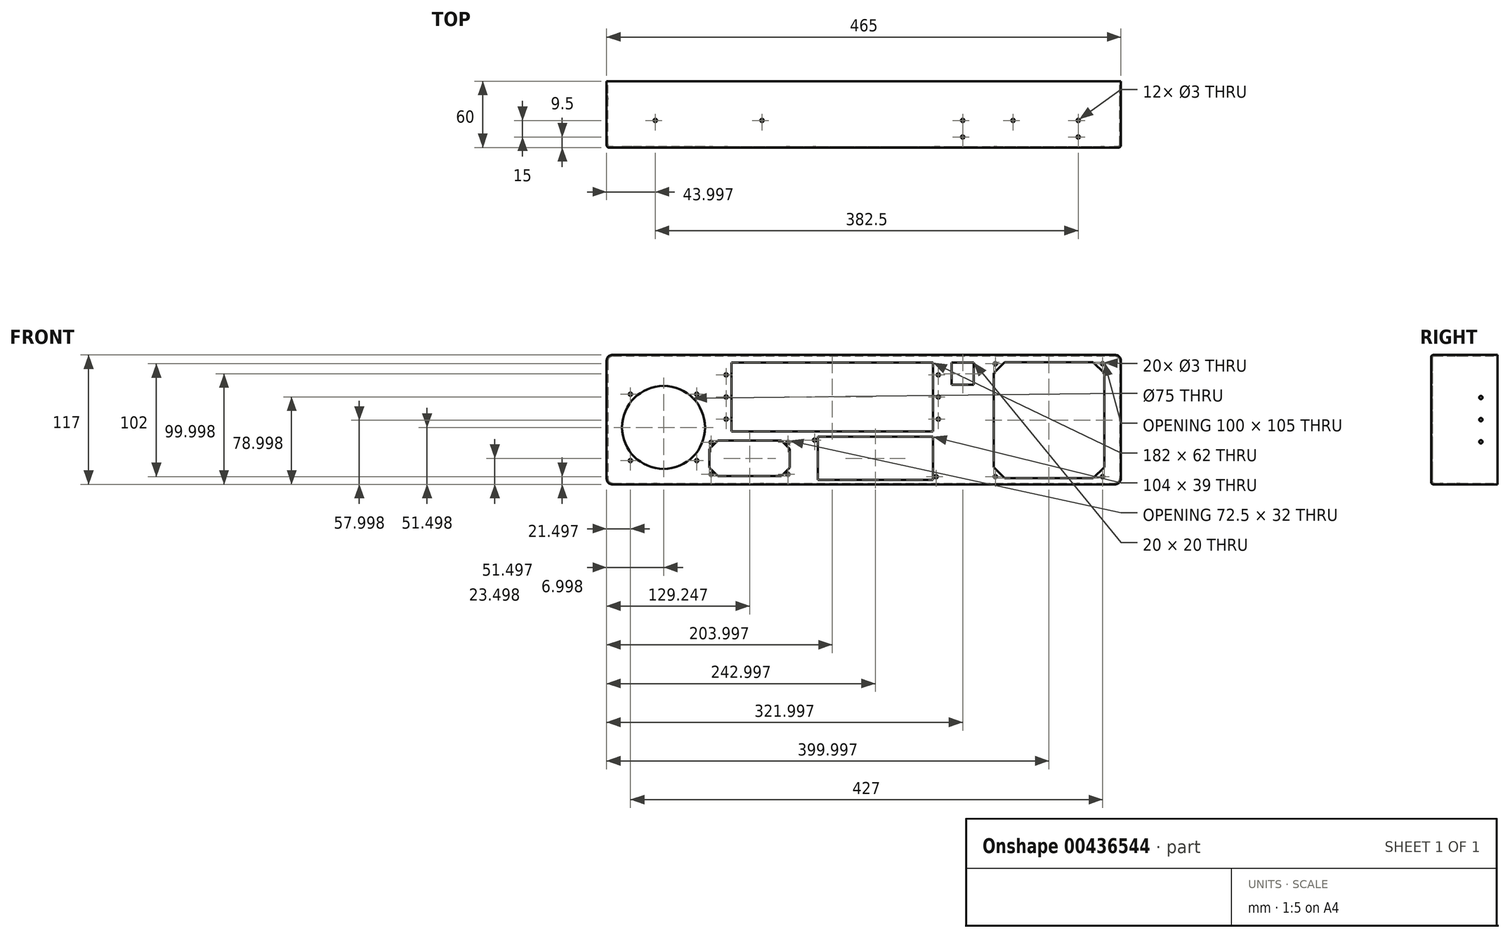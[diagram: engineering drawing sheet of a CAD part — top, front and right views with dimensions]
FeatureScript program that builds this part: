
annotation { "Feature Type Name" : "Feature", "Feature Type Description" : "" }
export const myFeature = defineFeature(function(context is Context, id is Id, definition is map)
    precondition{}
    {
        {
            var Q0;
            Q0=qCreatedBy(makeId("Front.planeOp"),FACE);
            var sketch = newSketch(context, id + "F0", { "sketchPlane" : qUnion([Q0])});
            skLineSegment(sketch, "E0.bottom", {"start": v(-245.15, 85.69) * mm, "end": v(219.85, 85.69) * mm});
            skLineSegment(sketch, "E0.top", {"start": v(-245.15, -31.31) * mm, "end": v(219.85, -31.31) * mm});
            skLineSegment(sketch, "E0.left", {"start": v(-245.15, 85.69) * mm, "end": v(-245.15, -31.31) * mm});
            skLineSegment(sketch, "E0.right", {"start": v(219.85, 85.69) * mm, "end": v(219.85, -31.31) * mm});
            skSolve(sketch);
        }
        {
            var Q0;
            Q0=qSketchRegion(id+"F0",true);
            var Q1;
            Q1=makeQuery(id+"F0.imprint","IMPRINT",FACE,{"disambiguationData":[TD([[makeQuery(id+"F0.imprint","IMPRINT",EDGE,{"derivedFrom":sQuery(id+"F0.wireOp",EDGE,"E0.bottom")}),-1.0]])]});
            extrude(context, id + "F1", {"entities" : qUnion([Q0, Q1]), "depth" : 60 * mm});
        }
        {
            var Q0;
            Q0=makeQuery(id+"F1.opExtrude","CAP_FACE",FACE,{"disambiguationData":[OSD([sQuery(id+"F0.wireOp",EDGE,"E0.bottom"),sQuery(id+"F0.wireOp",EDGE,"E0.top"),sQuery(id+"F0.wireOp",EDGE,"E0.left"),sQuery(id+"F0.wireOp",EDGE,"E0.right")])],"isStart":true});
            shell(context, id + "F2", {"entities" : qUnion([Q0]), "thickness" : 1 * mm});
        }
        {
            var Q0;
            Q0=makeQuery(id+"F1.opExtrude","CAP_FACE",FACE,{"disambiguationData":[OSD([sQuery(id+"F0.wireOp",EDGE,"E0.bottom"),sQuery(id+"F0.wireOp",EDGE,"E0.top"),sQuery(id+"F0.wireOp",EDGE,"E0.left"),sQuery(id+"F0.wireOp",EDGE,"E0.right")])],"isStart":false});
            var sketch = newSketch(context, id + "F3", { "sketchPlane" : qUnion([Q0])});
            skLineSegment(sketch, "E1.bottom", {"start": v(-132.15, 78.69) * mm, "end": v(49.85, 78.69) * mm});
            skLineSegment(sketch, "E1.top", {"start": v(-132.15, 16.69) * mm, "end": v(49.85, 16.69) * mm});
            skLineSegment(sketch, "E1.left", {"start": v(-132.15, 78.69) * mm, "end": v(-132.15, 16.69) * mm});
            skLineSegment(sketch, "E1.right", {"start": v(49.85, 78.69) * mm, "end": v(49.85, 16.69) * mm});
            skLineSegment(sketch, "E2.bottom", {"start": v(66.85, 78.69) * mm, "end": v(86.85, 78.69) * mm});
            skLineSegment(sketch, "E2.top", {"start": v(66.85, 58.69) * mm, "end": v(86.85, 58.69) * mm});
            skLineSegment(sketch, "E2.left", {"start": v(66.85, 78.69) * mm, "end": v(66.85, 58.69) * mm});
            skLineSegment(sketch, "E2.right", {"start": v(86.85, 78.69) * mm, "end": v(86.85, 58.69) * mm});
            skLineSegment(sketch, "E3.bottom", {"start": v(114.85, 79.19) * mm, "end": v(194.85, 79.19) * mm});
            skLineSegment(sketch, "E3.top", {"start": v(114.85, -25.81) * mm, "end": v(194.85, -25.81) * mm});
            skLineSegment(sketch, "E3.left", {"start": v(104.85, 69.19) * mm, "end": v(104.85, -15.81) * mm});
            skLineSegment(sketch, "E3.right", {"start": v(204.85, 69.19) * mm, "end": v(204.85, -15.81) * mm});
            skCircle(sketch, "E4", {"center": v(54.85, 67.69) * mm, "radius": 1.5 * mm});
            skCircle(sketch, "E5", {"center": v(54.85, 47.69) * mm, "radius": 1.5 * mm});
            skCircle(sketch, "E6", {"center": v(54.85, 27.69) * mm, "radius": 1.5 * mm});
            skCircle(sketch, "E7", {"center": v(106.35, 77.69) * mm, "radius": 1.5 * mm});
            skLineSegment(sketch, "E8", {"start": v(104.85, 69.19) * mm, "end": v(114.85, 79.19) * mm});
            skLineSegment(sketch, "E9.bottom", {"start": v(-144.65, 8.19) * mm, "end": v(-87.15, 8.19) * mm});
            skLineSegment(sketch, "E9.top", {"start": v(-144.65, -23.81) * mm, "end": v(-87.15, -23.81) * mm});
            skLineSegment(sketch, "E9.left", {"start": v(-152.15, 0.69) * mm, "end": v(-152.15, -16.31) * mm});
            skLineSegment(sketch, "E9.right", {"start": v(-79.65, 0.69) * mm, "end": v(-79.65, -16.31) * mm});
            skLineSegment(sketch, "E10", {"start": v(104.85, -15.81) * mm, "end": v(114.85, -25.81) * mm});
            skLineSegment(sketch, "E11", {"start": v(194.85, -25.81) * mm, "end": v(204.85, -15.81) * mm});
            skLineSegment(sketch, "E12", {"start": v(194.85, 79.19) * mm, "end": v(204.85, 69.19) * mm});
            skCircle(sketch, "E13", {"center": v(-193.65, 20.19) * mm, "radius": 37.5 * mm});
            skLineSegment(sketch, "E14", {"start": v(-152.15, 0.69) * mm, "end": v(-144.65, 8.19) * mm});
            skLineSegment(sketch, "E15", {"start": v(-87.15, 8.19) * mm, "end": v(-79.65, 0.69) * mm});
            skLineSegment(sketch, "E16", {"start": v(-79.65, -16.31) * mm, "end": v(-87.15, -23.81) * mm});
            skLineSegment(sketch, "E17", {"start": v(-152.15, -16.31) * mm, "end": v(-144.65, -23.81) * mm});
            skCircle(sketch, "E18", {"center": v(-137.15, 67.69) * mm, "radius": 1.5 * mm});
            skCircle(sketch, "E19", {"center": v(-137.15, 47.69) * mm, "radius": 1.5 * mm});
            skCircle(sketch, "E20", {"center": v(-137.15, 27.69) * mm, "radius": 1.5 * mm});
            skCircle(sketch, "E21", {"center": v(-223.65, 50.19) * mm, "radius": 1.5 * mm});
            skCircle(sketch, "E22", {"center": v(-223.65, -9.81) * mm, "radius": 1.5 * mm});
            skCircle(sketch, "E23", {"center": v(-163.65, -9.81) * mm, "radius": 1.5 * mm});
            skCircle(sketch, "E24", {"center": v(-163.65, 50.19) * mm, "radius": 1.5 * mm});
            skCircle(sketch, "E25", {"center": v(-57.15, 8.69) * mm, "radius": 1.5 * mm});
            skCircle(sketch, "E26", {"center": v(52.85, -24.31) * mm, "radius": 1.5 * mm});
            skLineSegment(sketch, "E27.bottom", {"start": v(-54.15, 11.69) * mm, "end": v(49.85, 11.69) * mm});
            skLineSegment(sketch, "E27.top", {"start": v(-54.15, -27.31) * mm, "end": v(49.85, -27.31) * mm});
            skLineSegment(sketch, "E27.left", {"start": v(-54.15, 11.69) * mm, "end": v(-54.15, -27.31) * mm});
            skLineSegment(sketch, "E27.right", {"start": v(49.85, 11.69) * mm, "end": v(49.85, -27.31) * mm});
            skLineSegment(sketch, "E28.bottom", {"start": v(-163.65, -9.81) * mm, "end": v(-223.65, -9.81) * mm, "construction": true});
            skLineSegment(sketch, "E28.top", {"start": v(-163.65, 50.19) * mm, "end": v(-223.65, 50.19) * mm, "construction": true});
            skLineSegment(sketch, "E28.left", {"start": v(-163.65, -9.81) * mm, "end": v(-163.65, 50.19) * mm, "construction": true});
            skLineSegment(sketch, "E28.right", {"start": v(-223.65, -9.81) * mm, "end": v(-223.65, 50.19) * mm, "construction": true});
            skCircle(sketch, "E29", {"center": v(-150.65, 6.69) * mm, "radius": 1.5 * mm});
            skCircle(sketch, "E30", {"center": v(-81.15, 6.69) * mm, "radius": 1.5 * mm});
            skCircle(sketch, "E31", {"center": v(-150.65, -22.31) * mm, "radius": 1.5 * mm});
            skCircle(sketch, "E32", {"center": v(-81.15, -22.31) * mm, "radius": 1.5 * mm});
            skCircle(sketch, "E33", {"center": v(203.35, 77.69) * mm, "radius": 1.5 * mm});
            skCircle(sketch, "E34", {"center": v(106.35, -24.31) * mm, "radius": 1.5 * mm});
            skCircle(sketch, "E35", {"center": v(203.35, -24.31) * mm, "radius": 1.5 * mm});
            skSolve(sketch);
        }
        {
            var Q0;
            Q0=qSketchRegion(id+"F3",true);
            extrude(context, id + "F4", {"entities" : qUnion([Q0]), "operationType" : NewBodyOperationType.REMOVE, "oppositeDirection" : true, "depth" : 25 * mm});
        }
        {
            var Q0;
            Q0=makeQuery(id+"F1.opExtrude","SWEPT_EDGE",EDGE,{"disambiguationData":[OSD([sQuery(id+"F0.wireOp",EDGE,"E0.bottom"),sQuery(id+"F0.wireOp",EDGE,"E0.left")])]});
            var Q1;
            Q1=makeQuery(id+"F1.opExtrude","SWEPT_EDGE",EDGE,{"disambiguationData":[OSD([sQuery(id+"F0.wireOp",EDGE,"E0.bottom"),sQuery(id+"F0.wireOp",EDGE,"E0.right")])]});
            var Q2;
            Q2=makeQuery(id+"F1.opExtrude","SWEPT_EDGE",EDGE,{"disambiguationData":[OSD([sQuery(id+"F0.wireOp",EDGE,"E0.top"),sQuery(id+"F0.wireOp",EDGE,"E0.right")])]});
            var Q3;
            Q3=makeQuery(id+"F1.opExtrude","SWEPT_EDGE",EDGE,{"disambiguationData":[OSD([sQuery(id+"F0.wireOp",EDGE,"E0.top"),sQuery(id+"F0.wireOp",EDGE,"E0.left")])]});
            var Q4;
            Q4=makeQuery(id+"F2.opShell","OFFSET_EDGE",EDGE,{"disambiguationData":[OSD([sQuery(id+"F0.wireOp",EDGE,"E0.bottom"),sQuery(id+"F0.wireOp",EDGE,"E0.left")])]});
            var Q5;
            Q5=makeQuery(id+"F2.opShell","OFFSET_EDGE",EDGE,{"disambiguationData":[OSD([sQuery(id+"F0.wireOp",EDGE,"E0.top"),sQuery(id+"F0.wireOp",EDGE,"E0.left")])]});
            var Q6;
            Q6=makeQuery(id+"F2.opShell","OFFSET_EDGE",EDGE,{"disambiguationData":[OSD([sQuery(id+"F0.wireOp",EDGE,"E0.top"),sQuery(id+"F0.wireOp",EDGE,"E0.right")])]});
            var Q7;
            Q7=makeQuery(id+"F2.opShell","OFFSET_EDGE",EDGE,{"disambiguationData":[OSD([sQuery(id+"F0.wireOp",EDGE,"E0.bottom"),sQuery(id+"F0.wireOp",EDGE,"E0.right")])]});
            fillet(context, id + "F5", {"entities" : qUnion([Q0, Q1, Q2, Q3, Q4, Q5, Q6, Q7]), "radius" : 5 * mm, "tangentPropagation" : true, "allowEdgeOverflow" : false});
        }
        {
            var Q0;
            {var subQ0=sQuery(id+"F0.wireOp",EDGE,"E0.right");var subQ1=sQuery(id+"F0.wireOp",EDGE,"E0.bottom");Q0=makeQuery(id+"F5.opFillet","BLEND_EDGE",EDGE,{"blendedFrom":[makeQuery(id+"F1.opExtrude","SWEPT_EDGE",EDGE,{"disambiguationData":[OSD([subQ1,subQ0])]}),makeQuery(id+"F1.opExtrude","CAP_FACE",FACE,{"disambiguationData":[OSD([subQ1,sQuery(id+"F0.wireOp",EDGE,"E0.top"),sQuery(id+"F0.wireOp",EDGE,"E0.left"),subQ0])],"isStart":false})],"blendedInto":[makeQuery(id+"F1.opExtrude","CAP_FACE",FACE,{"disambiguationData":[OSD([subQ1,sQuery(id+"F0.wireOp",EDGE,"E0.top"),sQuery(id+"F0.wireOp",EDGE,"E0.left"),subQ0])],"isStart":false})]});}
            var Q1;
            {var subQ0=sQuery(id+"F0.wireOp",EDGE,"E0.bottom");Q1=makeQuery(id+"F2.opShell","OFFSET_EDGE",EDGE,{"disambiguationData":[OSD([subQ0]),TDD([makeQuery(id+"F1.opExtrude","CAP_EDGE",EDGE,{"disambiguationData":[OSD([subQ0])],"isStart":false})])]});}
            fillet(context, id + "F6", {"entities" : qUnion([Q0, Q1]), "radius" : 2 * mm, "tangentPropagation" : true, "allowEdgeOverflow" : false});
        }
        {
            var Q0;
            Q0=makeQuery(id+"F1.opExtrude","SWEPT_FACE",FACE,{"disambiguationData":[OSD([sQuery(id+"F0.wireOp",EDGE,"E0.left")])]});
            var sketch = newSketch(context, id + "F7", { "sketchPlane" : qUnion([Q0])});
            skCircle(sketch, "E36", {"center": v(15, 47.19) * mm, "radius": 1.5 * mm});
            skCircle(sketch, "E37", {"center": v(15, 7.19) * mm, "radius": 1.5 * mm});
            skLineSegment(sketch, "E38", {"start": v(-16.01, 27.19) * mm, "end": v(37.35, 27.19) * mm, "construction": true});
            skPoint(sketch, "E39.middle.positionSnap0", {"position": v(0, 27.19) * mm});
            skPoint(sketch, "E39.centerSnap0", {"position": v(0, 27.19) * mm});
            skCircle(sketch, "E40", {"center": v(15, 27.19) * mm, "radius": 1.5 * mm});
            skSolve(sketch);
        }
        {
            var Q0;
            Q0=qSketchRegion(id+"F7",true);
            extrude(context, id + "F8", {"entities" : qUnion([Q0]), "operationType" : NewBodyOperationType.REMOVE, "oppositeDirection" : true, "depth" : 500 * mm});
        }
        {
            var Q0;
            Q0=makeQuery(id+"F1.opExtrude","SWEPT_FACE",FACE,{"disambiguationData":[OSD([sQuery(id+"F0.wireOp",EDGE,"E0.bottom")])]});
            var sketch = newSketch(context, id + "F9", { "sketchPlane" : qUnion([Q0])});
            skCircle(sketch, "E41", {"center": v(-201.15, -35.5) * mm, "radius": 1.5 * mm});
            skCircle(sketch, "E42", {"center": v(-104.65, -35.5) * mm, "radius": 1.5 * mm});
            skCircle(sketch, "E43", {"center": v(122.35, -35.5) * mm, "radius": 1.5 * mm});
            skCircle(sketch, "E44", {"center": v(181.35, -35.5) * mm, "radius": 1.5 * mm});
            skCircle(sketch, "E45", {"center": v(76.85, -35.5) * mm, "radius": 1.5 * mm});
            skCircle(sketch, "E46", {"center": v(76.85, -50.5) * mm, "radius": 1.5 * mm});
            skCircle(sketch, "E47", {"center": v(181.35, -50.5) * mm, "radius": 1.5 * mm});
            skSolve(sketch);
        }
        {
            var Q0;
            Q0=makeQuery(id+"F9.imprint","IMPRINT",FACE,{"disambiguationData":[TD([[makeQuery(id+"F9.imprint","IMPRINT",EDGE,{"derivedFrom":sQuery(id+"F9.wireOp",EDGE,"E41")}),1.0]])]});
            var Q1;
            Q1=makeQuery(id+"F9.imprint","IMPRINT",FACE,{"disambiguationData":[TD([[makeQuery(id+"F9.imprint","IMPRINT",EDGE,{"derivedFrom":sQuery(id+"F9.wireOp",EDGE,"E42")}),1.0]])]});
            var Q2;
            Q2=makeQuery(id+"F9.imprint","IMPRINT",FACE,{"disambiguationData":[TD([[makeQuery(id+"F9.imprint","IMPRINT",EDGE,{"derivedFrom":sQuery(id+"F9.wireOp",EDGE,"E43")}),1.0]])]});
            var Q3;
            Q3=makeQuery(id+"F9.imprint","IMPRINT",FACE,{"disambiguationData":[TD([[makeQuery(id+"F9.imprint","IMPRINT",EDGE,{"derivedFrom":sQuery(id+"F9.wireOp",EDGE,"E44")}),1.0]])]});
            var Q4;
            Q4=makeQuery(id+"F9.imprint","IMPRINT",FACE,{"disambiguationData":[TD([[makeQuery(id+"F9.imprint","IMPRINT",EDGE,{"derivedFrom":sQuery(id+"F9.wireOp",EDGE,"E47")}),1.0]])]});
            extrude(context, id + "F10", {"entities" : qUnion([Q0, Q1, Q2, Q3, Q4]), "operationType" : NewBodyOperationType.REMOVE, "endBound" : BoundingType.THROUGH_ALL, "oppositeDirection" : true, "depth" : 117 * mm});
        }
        {
            var Q0;
            Q0=makeQuery(id+"F9.imprint","IMPRINT",FACE,{"disambiguationData":[TD([[makeQuery(id+"F9.imprint","IMPRINT",EDGE,{"derivedFrom":sQuery(id+"F9.wireOp",EDGE,"E45")}),1.0]])]});
            var Q1;
            Q1=makeQuery(id+"F9.imprint","IMPRINT",FACE,{"disambiguationData":[TD([[makeQuery(id+"F9.imprint","IMPRINT",EDGE,{"derivedFrom":sQuery(id+"F9.wireOp",EDGE,"E46")}),1.0]])]});
            extrude(context, id + "F11", {"entities" : qUnion([Q0, Q1]), "operationType" : NewBodyOperationType.REMOVE, "oppositeDirection" : true, "depth" : 2 * mm});
        }
    });
